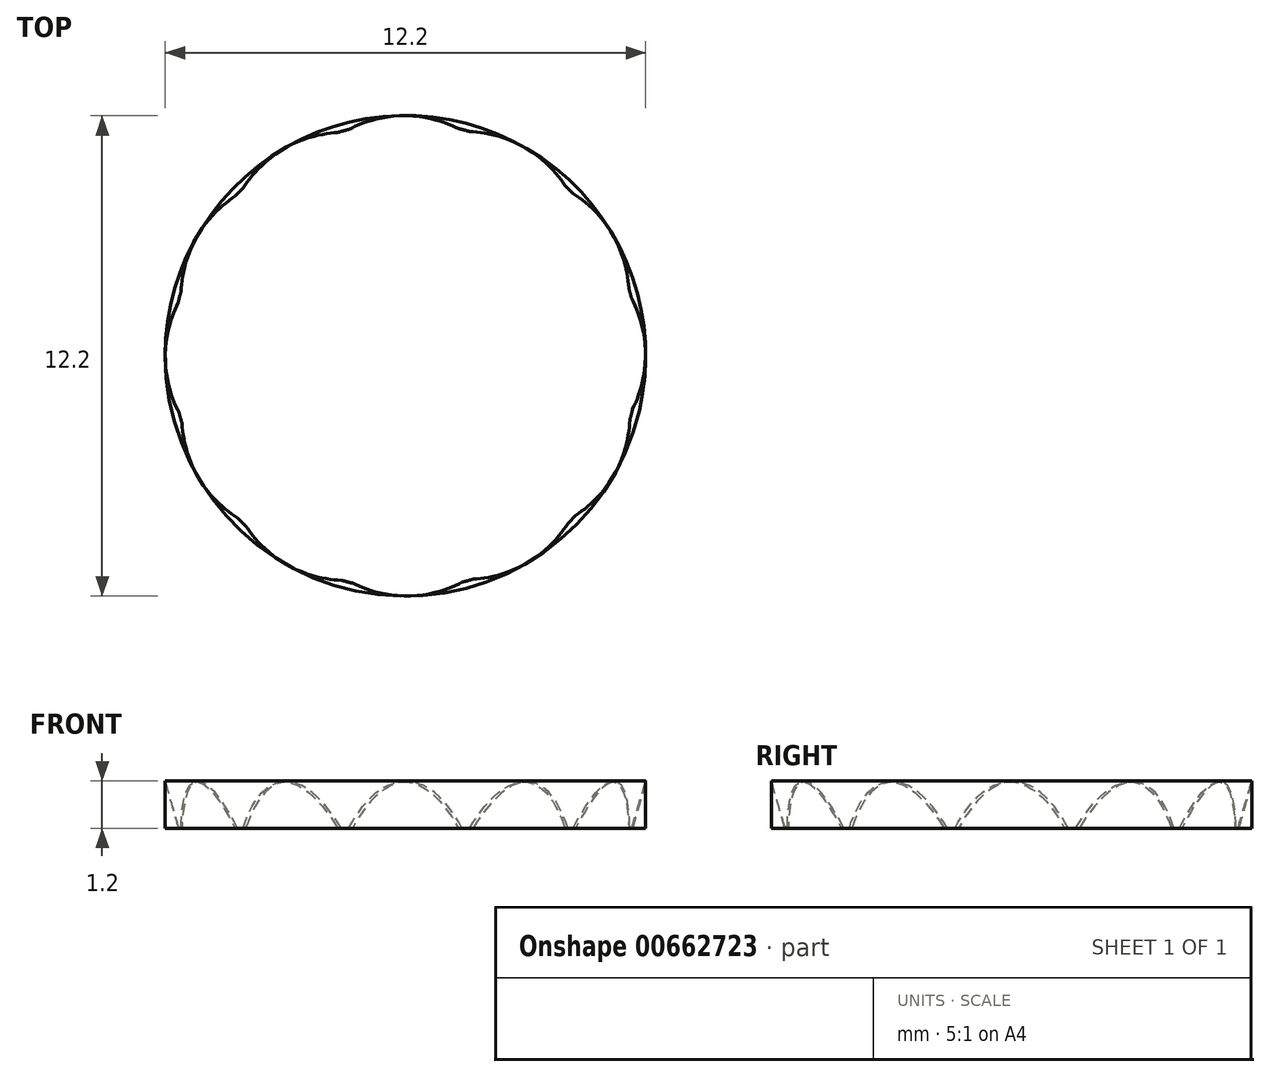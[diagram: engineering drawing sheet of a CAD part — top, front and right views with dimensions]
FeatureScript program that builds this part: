
annotation { "Feature Type Name" : "Feature", "Feature Type Description" : "" }
export const myFeature = defineFeature(function(context is Context, id is Id, definition is map)
    precondition{}
    {
        {
            var Q0;
            Q0=qCreatedBy(makeId("Top.planeOp"),FACE);
            var sketch = newSketch(context, id + "F0", { "sketchPlane" : qUnion([Q0])});
            skCircle(sketch, "E0", {"center": v(0, 0) * mm, "radius": 6.1 * mm});
            skPoint(sketch, "E1", {"position": v(6.1, 0) * mm});
            skPoint(sketch, "E2", {"position": v(5.88, 0) * mm});
            skSolve(sketch);
        }
        {
            var Q0;
            Q0=qCreatedBy(makeId("Front.planeOp"),FACE);
            var sketch = newSketch(context, id + "F1", { "sketchPlane" : qUnion([Q0])});
            skLineSegment(sketch, "E3", {"start": v(5.93, 0) * mm, "end": v(6.1, 0) * mm});
            skLineSegment(sketch, "E4", {"start": v(6.1, 0) * mm, "end": v(6.1, 1.2) * mm});
            skLineSegment(sketch, "E5", {"start": v(6.1, 1.2) * mm, "end": v(5.93, 0) * mm});
            skSolve(sketch);
        }
        {
            var Q0;
            Q0=makeQuery(id+"F1.imprint","IMPRINT",FACE,{"disambiguationData":[TD([[makeQuery(id+"F1.imprint","IMPRINT",EDGE,{"derivedFrom":sQuery(id+"F1.wireOp",EDGE,"E3")}),1.0]])]});
            var Q1;
            Q1=sQuery(id+"F0.wireOp",EDGE,"E0");
            revolve(context, id + "F2", {"entities" : qUnion([Q0]), "axis" : qUnion([Q1]), "revolveType" : RevolveType.FULL});
        }
        {
            var Q0;
            Q0=qCreatedBy(makeId("Top.planeOp"),FACE);
            var sketch = newSketch(context, id + "F3", { "sketchPlane" : qUnion([Q0])});
            skCircle(sketch, "E6", {"center": v(-0.03, 3.05) * mm, "radius": 3.05 * mm});
            skPoint(sketch, "E6.first.point", {"position": v(0, 6.1) * mm});
            skPoint(sketch, "E6.second.point", {"position": v(0, 0) * mm});
            skPoint(sketch, "E6.third.point", {"position": v(3.02, 3.07) * mm});
            skSolve(sketch);
        }
        {
            var Q0;
            Q0=makeQuery(id+"F3.imprint","IMPRINT",FACE,{"disambiguationData":[TD([[makeQuery(id+"F3.imprint","IMPRINT",EDGE,{"derivedFrom":sQuery(id+"F3.wireOp",EDGE,"E6")}),1.0]])]});
            extrude(context, id + "F4", {"entities" : qUnion([Q0]), "depth" : 2 * mm, "offsetDistance" : 25 * mm});
        }
        {
            var Q0;
            Q0=makeQuery(id+"F4.opExtrude","SWEPT_BODY",BODY,{"disambiguationData":[OSD([sQuery(id+"F3.wireOp",EDGE,"E6")])]});
            var Q1;
            Q1=makeQuery(id+"F2.opRevolve","SWEPT_EDGE",EDGE,{"disambiguationData":[OSD([sQuery(id+"F1.wireOp",EDGE,"E3"),sQuery(id+"F1.wireOp",EDGE,"E4")])]});
            circularPattern(context, id + "F5", {"operationType" : NewBodyOperationType.REMOVE, "entities" : qUnion([Q0]), "axis" : qUnion([Q1]), "angle" : 360 * degree, "instanceCount" : 12, "equalSpace" : true});
        }
    });
